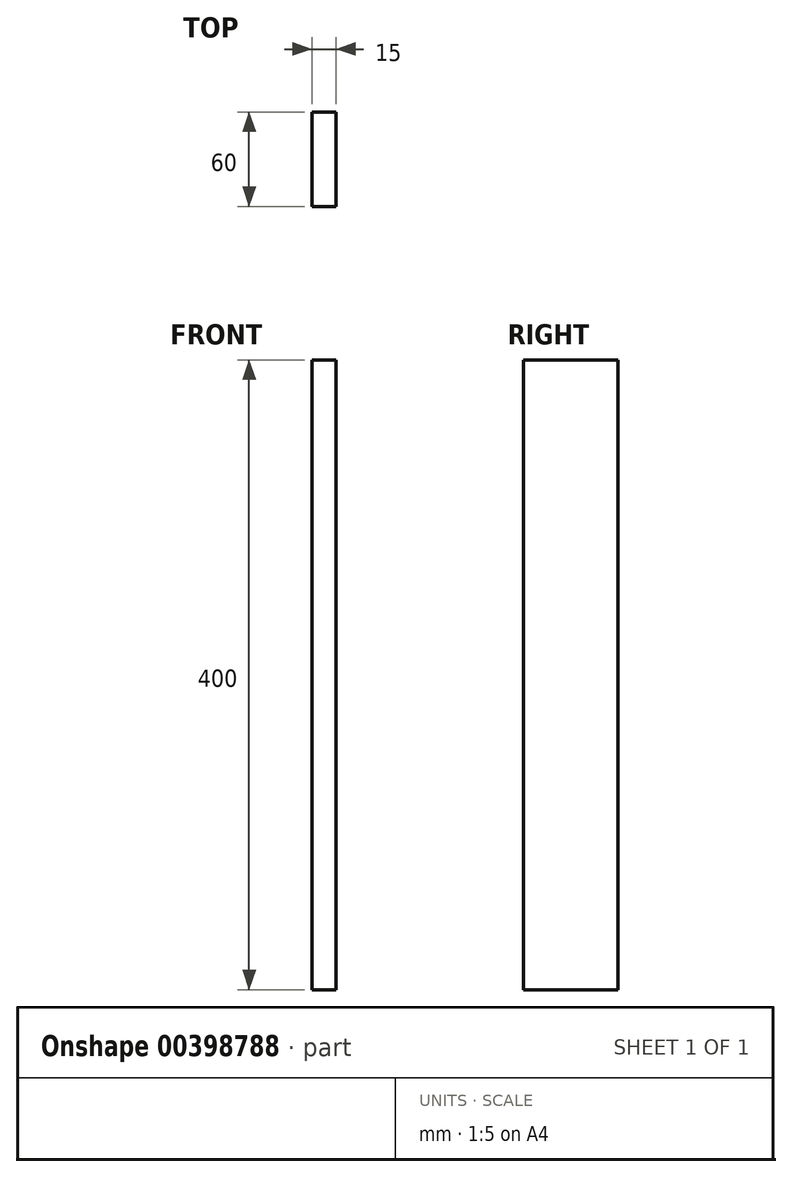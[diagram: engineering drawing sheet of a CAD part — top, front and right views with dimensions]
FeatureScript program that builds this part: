
annotation { "Feature Type Name" : "Feature", "Feature Type Description" : "" }
export const myFeature = defineFeature(function(context is Context, id is Id, definition is map)
    precondition{}
    {
        {
            var Q0;
            Q0=qCreatedBy(makeId("Right.planeOp"),FACE);
            var sketch = newSketch(context, id + "F0", { "sketchPlane" : qUnion([Q0])});
            skLineSegment(sketch, "E0.bottom", {"start": v(30, 200) * mm, "end": v(-30, 200) * mm});
            skLineSegment(sketch, "E0.top", {"start": v(30, -200) * mm, "end": v(-30, -200) * mm});
            skLineSegment(sketch, "E0.left", {"start": v(30, 200) * mm, "end": v(30, -200) * mm});
            skLineSegment(sketch, "E0.right", {"start": v(-30, 200) * mm, "end": v(-30, -200) * mm});
            skPoint(sketch, "E0.middle", {"position": v(0, 0) * mm});
            skSolve(sketch);
        }
        {
            var Q0;
            Q0=makeQuery(id+"F0.imprint","IMPRINT",FACE,{"disambiguationData":[TD([[makeQuery(id+"F0.imprint","IMPRINT",EDGE,{"derivedFrom":sQuery(id+"F0.wireOp",EDGE,"E0.bottom")}),1.0]])]});
            extrude(context, id + "F1", {"entities" : qUnion([Q0]), "depth" : 15 * mm, "offsetDistance" : 25 * mm});
        }
    });
